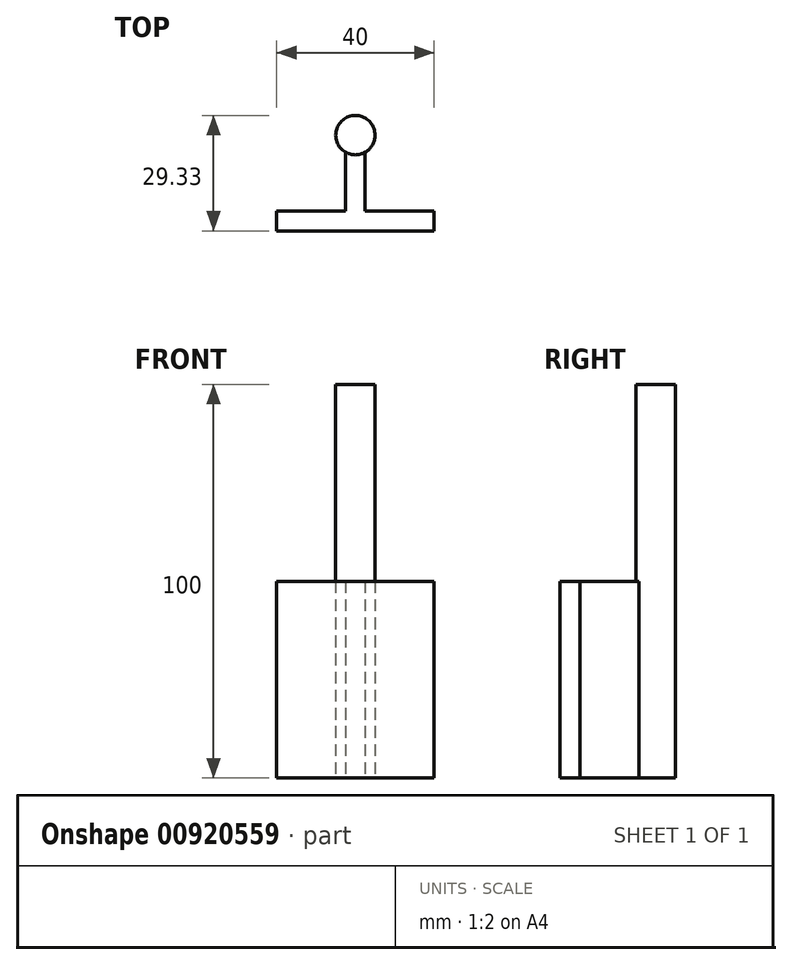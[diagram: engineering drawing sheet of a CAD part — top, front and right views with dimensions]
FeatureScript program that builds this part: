
annotation { "Feature Type Name" : "Feature", "Feature Type Description" : "" }
export const myFeature = defineFeature(function(context is Context, id is Id, definition is map)
    precondition{}
    {
        {
            var Q0;
            Q0=qCreatedBy(makeId("Top.planeOp"),FACE);
            var sketch = newSketch(context, id + "F0", { "sketchPlane" : qUnion([Q0])});
            skLineSegment(sketch, "E0.bottom", {"start": v(-20, 5) * mm, "end": v(20, 5) * mm});
            skLineSegment(sketch, "E0.top", {"start": v(-20, 0) * mm, "end": v(20, 0) * mm});
            skLineSegment(sketch, "E0.left", {"start": v(-20, 5) * mm, "end": v(-20, 0) * mm});
            skLineSegment(sketch, "E0.right", {"start": v(20, 5) * mm, "end": v(20, 0) * mm});
            skLineSegment(sketch, "E1.bottom", {"start": v(-2.5, 5) * mm, "end": v(2.5, 5) * mm});
            skLineSegment(sketch, "E1.top", {"start": v(-2.5, 20) * mm, "end": v(2.5, 20) * mm});
            skLineSegment(sketch, "E1.left", {"start": v(-2.5, 5) * mm, "end": v(-2.5, 20) * mm});
            skLineSegment(sketch, "E1.right", {"start": v(2.5, 5) * mm, "end": v(2.5, 20) * mm});
            skCircle(sketch, "E2", {"center": v(0, 24.33) * mm, "radius": 5 * mm});
            skSolve(sketch);
        }
        {
            var Q0;
            Q0=makeQuery(id+"F0.imprint","IMPRINT",FACE,{"disambiguationData":[TD([[makeQuery(id+"F0.imprint","IMPRINT",EDGE,{"derivedFrom":sQuery(id+"F0.wireOp",EDGE,"E0.top")}),1.0]])]});
            var Q1;
            {var subQ2=sQuery(id+"F0.wireOp",EDGE,"E1.left");Q1=makeQuery(id+"F0.imprint","IMPRINT",FACE,{"disambiguationData":[TD([[makeQuery(id+"F0.imprint","IMPRINT",EDGE,{"derivedFrom":subQ2}),-1.0]])]});}
            var Q2;
            {var subQ0=sQuery(id+"F0.wireOp",EDGE,"E1.top");Q2=makeQuery(id+"F0.imprint","IMPRINT",FACE,{"disambiguationData":[TD([[makeQuery(id+"F0.imprint","IMPRINT",EDGE,{"derivedFrom":subQ0}),1.0]])]});}
            var Q3;
            {var subQ0=sQuery(id+"F0.wireOp",EDGE,"E1.top");Q3=makeQuery(id+"F0.imprint","IMPRINT",FACE,{"disambiguationData":[TD([[makeQuery(id+"F0.imprint","IMPRINT",EDGE,{"derivedFrom":subQ0}),-1.0]])]});}
            extrude(context, id + "F1", {"entities" : qUnion([Q0, Q1, Q2, Q3]), "depth" : 50 * mm, "offsetDistance" : 25 * mm});
        }
        {
            var Q0;
            {var subQ0=sQuery(id+"F0.wireOp",EDGE,"E1.top");Q0=makeQuery(id+"F0.imprint","IMPRINT",FACE,{"disambiguationData":[TD([[makeQuery(id+"F0.imprint","IMPRINT",EDGE,{"derivedFrom":subQ0}),-1.0]])]});}
            var Q1;
            {var subQ0=sQuery(id+"F0.wireOp",EDGE,"E1.top");Q1=makeQuery(id+"F0.imprint","IMPRINT",FACE,{"disambiguationData":[TD([[makeQuery(id+"F0.imprint","IMPRINT",EDGE,{"derivedFrom":subQ0}),1.0]])]});}
            extrude(context, id + "F2", {"entities" : qUnion([Q0, Q1]), "operationType" : NewBodyOperationType.ADD, "depth" : 100 * mm, "offsetDistance" : 25 * mm});
        }
    });
